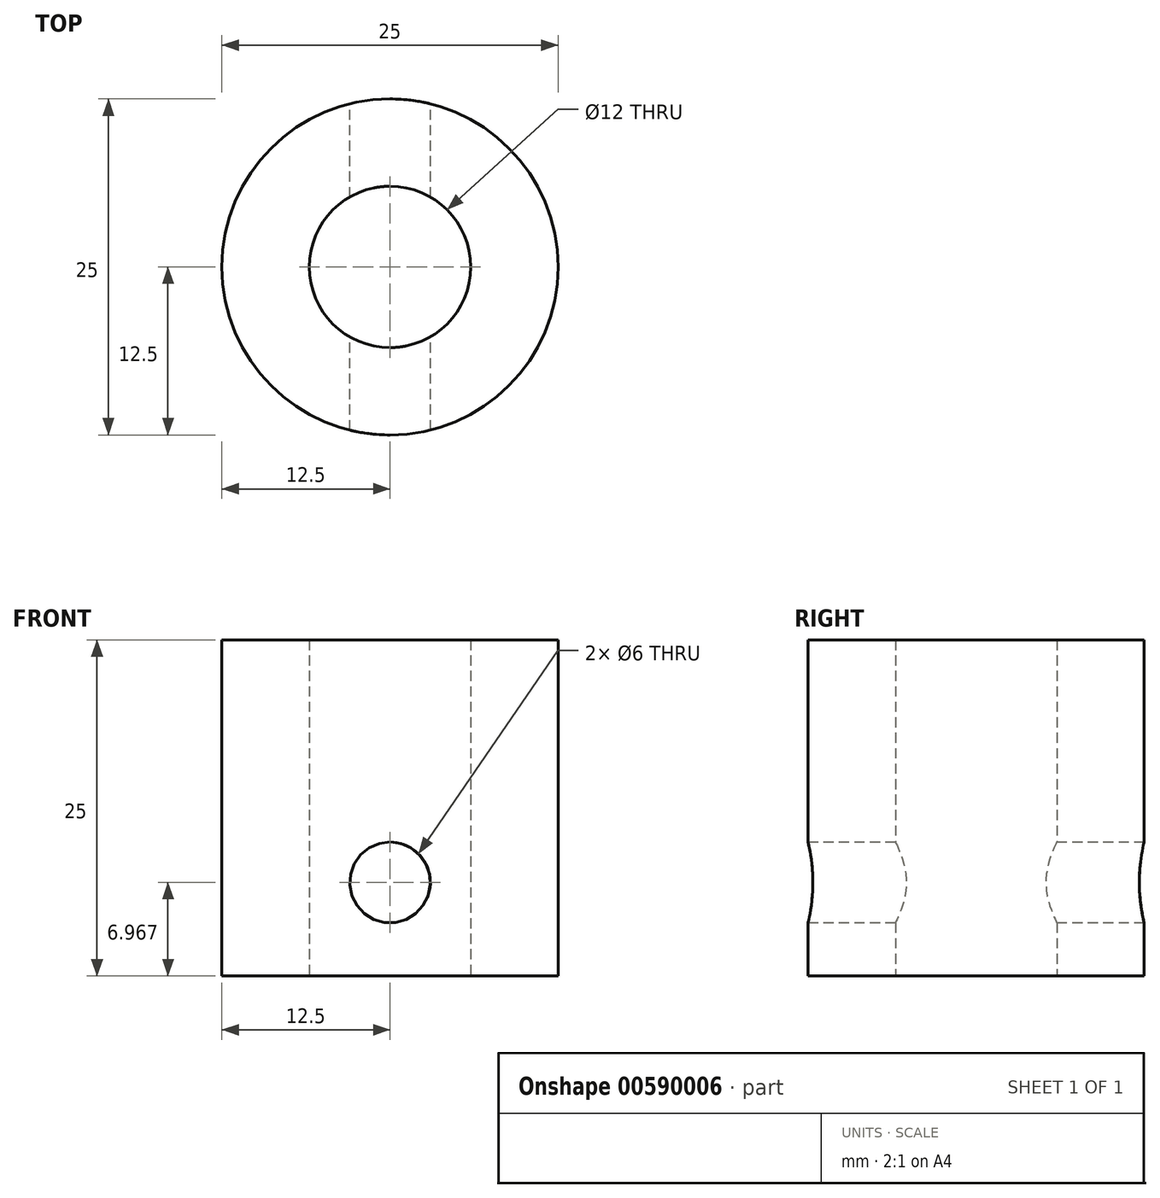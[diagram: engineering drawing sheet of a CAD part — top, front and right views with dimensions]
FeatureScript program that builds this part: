
annotation { "Feature Type Name" : "Feature", "Feature Type Description" : "" }
export const myFeature = defineFeature(function(context is Context, id is Id, definition is map)
    precondition{}
    {
        {
            var Q0;
            Q0=qCreatedBy(makeId("Top.planeOp"),FACE);
            var sketch = newSketch(context, id + "F0", { "sketchPlane" : qUnion([Q0])});
            skCircle(sketch, "E0", {"center": v(0, 0) * mm, "radius": 6 * mm});
            skCircle(sketch, "E1", {"center": v(0, 0) * mm, "radius": 12.5 * mm});
            skSolve(sketch);
        }
        {
            var Q0;
            Q0 = qSketchRegion(id + "F0", true);
            extrude(context, id + "F1", {"entities" : qUnion([Q0]), "depth" : 25 * mm, "offsetDistance" : 25 * mm});
        }
        {
            var Q0;
            Q0=qCreatedBy(makeId("Front.planeOp"),FACE);
            var sketch = newSketch(context, id + "F2", { "sketchPlane" : qUnion([Q0])});
            skCircle(sketch, "E2", {"center": v(0, 6.97) * mm, "radius": 3 * mm});
            skSolve(sketch);
        }
        {
            var Q0;
            Q0 = qSketchRegion(id + "F2", true);
            extrude(context, id + "F3", {"entities" : qUnion([Q0]), "operationType" : NewBodyOperationType.REMOVE, "depth" : 25 * mm, "offsetDistance" : 25 * mm, "symmetric" : true});
        }
    });
